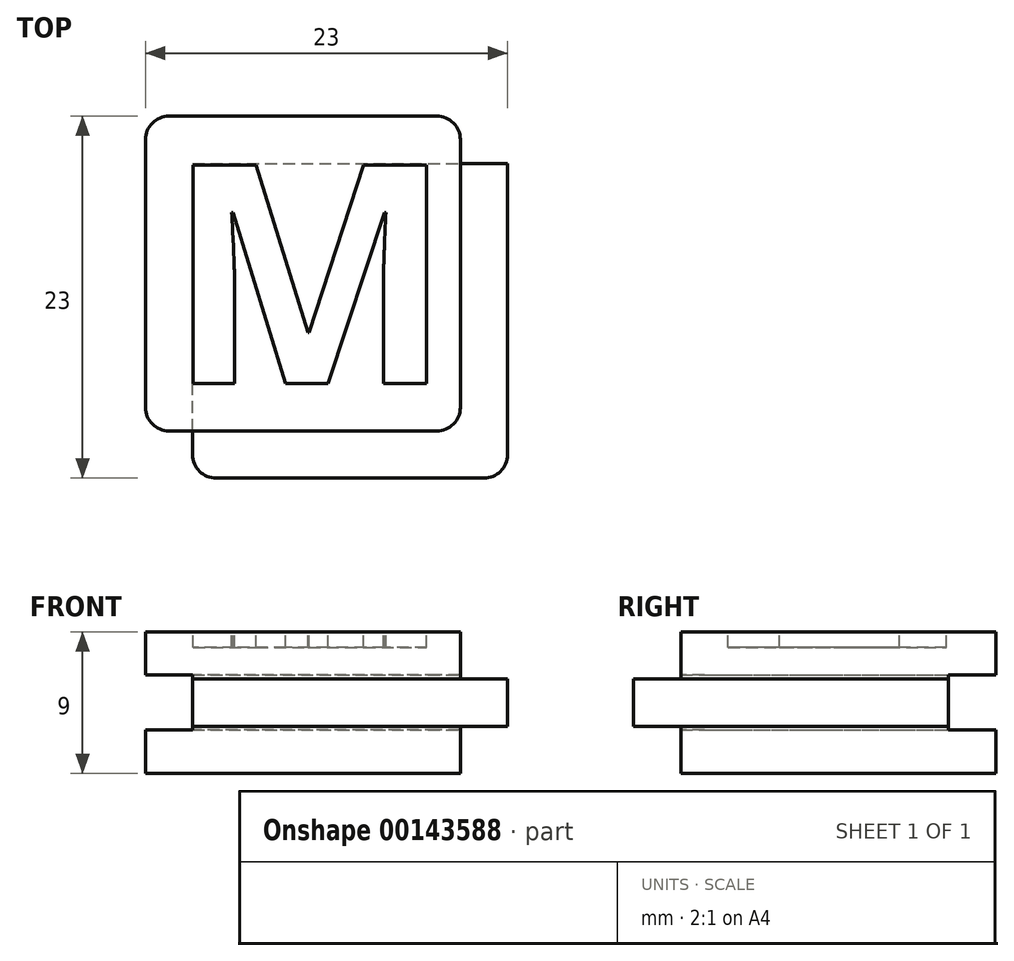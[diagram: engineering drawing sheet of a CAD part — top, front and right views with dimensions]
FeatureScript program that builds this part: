
annotation { "Feature Type Name" : "Feature", "Feature Type Description" : "" }
export const myFeature = defineFeature(function(context is Context, id is Id, definition is map)
    precondition{}
    {
        {
            var Q0;
            Q0=qCreatedBy(makeId("Front.planeOp"),FACE);
            var sketch = newSketch(context, id + "F0", { "sketchPlane" : qUnion([Q0])});
            skLineSegment(sketch, "E0.bottom", {"start": v(10, 4.5) * mm, "end": v(-10, 4.5) * mm});
            skLineSegment(sketch, "E0.top", {"start": v(10, -4.5) * mm, "end": v(-10, -4.5) * mm});
            skLineSegment(sketch, "E0.left", {"start": v(10, 4.5) * mm, "end": v(10, -4.5) * mm});
            skLineSegment(sketch, "E0.right", {"start": v(-10, 4.5) * mm, "end": v(-10, -4.5) * mm});
            skPoint(sketch, "E0.middle", {"position": v(0, 0) * mm});
            skLineSegment(sketch, "E1.bottom", {"start": v(13, 1.5) * mm, "end": v(7, 1.5) * mm});
            skLineSegment(sketch, "E1.top", {"start": v(13, -1.5) * mm, "end": v(7, -1.5) * mm});
            skLineSegment(sketch, "E1.left", {"start": v(13, 1.5) * mm, "end": v(13, -1.5) * mm});
            skLineSegment(sketch, "E1.right", {"start": v(7, 1.5) * mm, "end": v(7, -1.5) * mm});
            skPoint(sketch, "E1.middle", {"position": v(10, 0) * mm});
            skLineSegment(sketch, "E2.bottom", {"start": v(7, 1.5) * mm, "end": v(-7, 1.5) * mm});
            skLineSegment(sketch, "E2.top", {"start": v(7, -1.5) * mm, "end": v(-7, -1.5) * mm});
            skLineSegment(sketch, "E2.right", {"start": v(-7, 1.5) * mm, "end": v(-7, -1.5) * mm});
            skLineSegment(sketch, "E3.bottom", {"start": v(-7, -1.5) * mm, "end": v(-10, -1.5) * mm});
            skLineSegment(sketch, "E3.top", {"start": v(-7, 1.5) * mm, "end": v(-10, 1.5) * mm});
            skLineSegment(sketch, "E3.left", {"start": v(-7, -1.5) * mm, "end": v(-7, 1.5) * mm});
            skLineSegment(sketch, "E3.right", {"start": v(-10, -1.5) * mm, "end": v(-10, 1.5) * mm});
            skSolve(sketch);
        }
        {
            var Q0;
            {var subQ5=sQuery(id+"F0.wireOp",EDGE,"E0.bottom");Q0=makeQuery(id+"F0.imprint","IMPRINT",FACE,{"disambiguationData":[TD([[makeQuery(id+"F0.imprint","IMPRINT",EDGE,{"derivedFrom":subQ5}),1.0]])]});}
            var Q1;
            Q1=makeQuery(id+"F0.imprint","IMPRINT",FACE,{"disambiguationData":[TD([[makeQuery(id+"F0.imprint","IMPRINT",EDGE,{"derivedFrom":sQuery(id+"F0.wireOp",EDGE,"E2.bottom")}),1.0]])]});
            var Q2;
            {var subQ5=sQuery(id+"F0.wireOp",EDGE,"E1.left");Q2=makeQuery(id+"F0.imprint","IMPRINT",FACE,{"disambiguationData":[TD([[makeQuery(id+"F0.imprint","IMPRINT",EDGE,{"derivedFrom":subQ5}),-1.0]])]});}
            var Q3;
            {var subQ5=sQuery(id+"F0.wireOp",EDGE,"E1.right");Q3=makeQuery(id+"F0.imprint","IMPRINT",FACE,{"disambiguationData":[TD([[makeQuery(id+"F0.imprint","IMPRINT",EDGE,{"derivedFrom":subQ5}),1.0]])]});}
            var Q4;
            Q4=makeQuery(id+"F0.imprint","IMPRINT",FACE,{"disambiguationData":[TD([[makeQuery(id+"F0.imprint","IMPRINT",EDGE,{"derivedFrom":sQuery(id+"F0.wireOp",EDGE,"E3.bottom")}),-1.0]])]});
            var Q5;
            {var subQ5=sQuery(id+"F0.wireOp",EDGE,"E0.top");Q5=makeQuery(id+"F0.imprint","IMPRINT",FACE,{"disambiguationData":[TD([[makeQuery(id+"F0.imprint","IMPRINT",EDGE,{"derivedFrom":subQ5}),-1.0]])]});}
            extrude(context, id + "F1", {"entities" : qUnion([Q0, Q1, Q2, Q3, Q4, Q5]), "oppositeDirection" : true, "depth" : 20 * mm});
        }
        {
            var Q0;
            Q0=makeQuery(id+"F0.imprint","IMPRINT",FACE,{"disambiguationData":[TD([[makeQuery(id+"F0.imprint","IMPRINT",EDGE,{"derivedFrom":sQuery(id+"F0.wireOp",EDGE,"E3.bottom")}),-1.0]])]});
            var Q1;
            Q1=makeQuery(id+"F0.imprint","IMPRINT",FACE,{"disambiguationData":[TD([[makeQuery(id+"F0.imprint","IMPRINT",EDGE,{"derivedFrom":sQuery(id+"F0.wireOp",EDGE,"E2.bottom")}),1.0]])]});
            var Q2;
            {var subQ5=sQuery(id+"F0.wireOp",EDGE,"E1.right");Q2=makeQuery(id+"F0.imprint","IMPRINT",FACE,{"disambiguationData":[TD([[makeQuery(id+"F0.imprint","IMPRINT",EDGE,{"derivedFrom":subQ5}),1.0]])]});}
            var Q3;
            {var subQ5=sQuery(id+"F0.wireOp",EDGE,"E1.left");Q3=makeQuery(id+"F0.imprint","IMPRINT",FACE,{"disambiguationData":[TD([[makeQuery(id+"F0.imprint","IMPRINT",EDGE,{"derivedFrom":subQ5}),-1.0]])]});}
            extrude(context, id + "F2", {"entities" : qUnion([Q0, Q1, Q2, Q3]), "operationType" : NewBodyOperationType.ADD, "depth" : 3 * mm});
        }
        {
            var Q0;
            {var subQ0=sQuery(id+"F0.wireOp",EDGE,"E1.left");Q0=makeQuery(id+"F2.boolean.opBoolean","MERGE",FACE,{"derivedFrom":[makeQuery(id+"F1.opExtrude","SWEPT_FACE",FACE,{"disambiguationData":[OSD([subQ0])]}),makeQuery(id+"F2.opExtrude","SWEPT_FACE",FACE,{"disambiguationData":[OSD([subQ0])]})]});}
            var sketch = newSketch(context, id + "F3", { "sketchPlane" : qUnion([Q0])});
            skLineSegment(sketch, "E4.bottom", {"start": v(23, 1.75) * mm, "end": v(17, 1.75) * mm});
            skLineSegment(sketch, "E4.top", {"start": v(23, -1.75) * mm, "end": v(17, -1.75) * mm});
            skLineSegment(sketch, "E4.left", {"start": v(23, 1.75) * mm, "end": v(23, -1.75) * mm});
            skLineSegment(sketch, "E4.right", {"start": v(17, 1.75) * mm, "end": v(17, -1.75) * mm});
            skPoint(sketch, "E4.middle", {"position": v(20, 0) * mm});
            skSolve(sketch);
        }
        {
            var Q0;
            {var subQ1=sQuery(id+"F3.wireOp",EDGE,"E4.bottom");Q0=makeQuery(id+"F3.imprint","IMPRINT",FACE,{"disambiguationData":[TD([[makeQuery(id+"F3.imprint","IMPRINT",EDGE,{"derivedFrom":subQ1}),1.0]])]});}
            var Q1;
            {var subQ1=sQuery(id+"F0.wireOp",EDGE,"E1.left");var subQ8=makeQuery(id+"F1.opExtrude","CAP_EDGE",EDGE,{"disambiguationData":[OSD([subQ1])],"isStart":false});Q1=makeQuery(id+"F3.imprint","IMPRINT",FACE,{"disambiguationData":[TD([[makeQuery(id+"F3.imprint","IMPRINT",EDGE,{"derivedFrom":subQ8}),-1.0]])]});}
            extrude(context, id + "F4", {"entities" : qUnion([Q0, Q1]), "operationType" : NewBodyOperationType.REMOVE, "oppositeDirection" : true, "depth" : 100 * mm});
        }
        {
            var Q0;
            Q0=makeQuery(id+"F4.boolean.opBoolean","COPY",FACE,{"derivedFrom":makeQuery(id+"F4.opExtrude","SWEPT_FACE",FACE,{"disambiguationData":[OSD([sQuery(id+"F3.wireOp",EDGE,"E4.right")])]})});
            var sketch = newSketch(context, id + "F5", { "sketchPlane" : qUnion([Q0])});
            skLineSegment(sketch, "E5.bottom", {"start": v(13, 1.75) * mm, "end": v(7, 1.75) * mm});
            skLineSegment(sketch, "E5.top", {"start": v(13, -1.75) * mm, "end": v(7, -1.75) * mm});
            skLineSegment(sketch, "E5.left", {"start": v(13, 1.75) * mm, "end": v(13, -1.75) * mm});
            skLineSegment(sketch, "E5.right", {"start": v(7, 1.75) * mm, "end": v(7, -1.75) * mm});
            skPoint(sketch, "E5.middle", {"position": v(10, 0) * mm});
            skSolve(sketch);
        }
        {
            var Q0;
            {var subQ3=sQuery(id+"F5.wireOp",EDGE,"E5.left");Q0=makeQuery(id+"F5.imprint","IMPRINT",FACE,{"disambiguationData":[TD([[makeQuery(id+"F5.imprint","IMPRINT",EDGE,{"derivedFrom":subQ3}),-1.0]])]});}
            var Q1;
            {var subQ4=sQuery(id+"F5.wireOp",EDGE,"E5.right");Q1=makeQuery(id+"F5.imprint","IMPRINT",FACE,{"disambiguationData":[TD([[makeQuery(id+"F5.imprint","IMPRINT",EDGE,{"derivedFrom":subQ4}),1.0]])]});}
            extrude(context, id + "F6", {"entities" : qUnion([Q0, Q1]), "operationType" : NewBodyOperationType.REMOVE, "oppositeDirection" : true, "depth" : 100 * mm});
        }
        {
            var Q0;
            Q0=makeQuery(id+"F6.boolean.opBoolean","INTERSECT",EDGE,{"derivedFrom":[makeQuery(id+"F2.opExtrude","CAP_FACE",FACE,{"disambiguationData":[OSD([sQuery(id+"F0.wireOp",EDGE,"E1.bottom"),sQuery(id+"F0.wireOp",EDGE,"E1.top"),sQuery(id+"F0.wireOp",EDGE,"E1.left"),sQuery(id+"F0.wireOp",EDGE,"E2.bottom"),sQuery(id+"F0.wireOp",EDGE,"E2.top"),sQuery(id+"F0.wireOp",EDGE,"E3.bottom"),sQuery(id+"F0.wireOp",EDGE,"E3.top"),sQuery(id+"F0.wireOp",EDGE,"E3.right")])],"isStart":false}),makeQuery(id+"F6.opExtrude","SWEPT_FACE",FACE,{"disambiguationData":[OSD([sQuery(id+"F5.wireOp",EDGE,"E5.right")])]})]});
            var Q1;
            Q1=makeQuery(id+"F2.opExtrude","CAP_EDGE",EDGE,{"disambiguationData":[OSD([sQuery(id+"F0.wireOp",EDGE,"E1.left")])],"isStart":false});
            var Q2;
            {var subQ0=sQuery(id+"F0.wireOp",EDGE,"E0.left");Q2=makeQuery(id+"F1.opExtrude","CAP_EDGE",EDGE,{"disambiguationData":[OSD([subQ0]),TDD([makeQuery(id+"F0.imprint","IMPRINT",EDGE,{"disambiguationData":[TD([[makeQuery(id+"F0.imprint","INTERSECT",VERTEX,{"derivedFrom":[sQuery(id+"F0.wireOp",EDGE,"E0.bottom"),subQ0]}),-1.0]])],"derivedFrom":subQ0})])],"isStart":true});}
            var Q3;
            {var subQ0=sQuery(id+"F0.wireOp",EDGE,"E0.left");Q3=makeQuery(id+"F1.opExtrude","CAP_EDGE",EDGE,{"disambiguationData":[OSD([subQ0]),TDD([makeQuery(id+"F0.imprint","IMPRINT",EDGE,{"disambiguationData":[TD([[makeQuery(id+"F0.imprint","INTERSECT",VERTEX,{"derivedFrom":[sQuery(id+"F0.wireOp",EDGE,"E0.top"),subQ0]}),1.0]])],"derivedFrom":subQ0})])],"isStart":true});}
            var Q4;
            {var subQ0=sQuery(id+"F0.wireOp",EDGE,"E3.right");var subQ1=sQuery(id+"F0.wireOp",EDGE,"E0.right");var subQ3=sQuery(id+"F0.wireOp",EDGE,"E0.top");Q4=makeQuery(id+"F2.boolean.opBoolean","SPLIT",EDGE,{"disambiguationData":[TD([makeQuery(id+"F1.opExtrude","SWEPT_FACE",FACE,{"disambiguationData":[OSD([subQ3])]})])],"derivedFrom":makeQuery(id+"F1.opExtrude","CAP_EDGE",EDGE,{"disambiguationData":[OSD([subQ1,subQ0])],"isStart":true})});}
            var Q5;
            {var subQ1=sQuery(id+"F0.wireOp",EDGE,"E3.right");var subQ2=sQuery(id+"F0.wireOp",EDGE,"E0.right");var subQ3=sQuery(id+"F0.wireOp",EDGE,"E0.bottom");Q5=makeQuery(id+"F2.boolean.opBoolean","SPLIT",EDGE,{"disambiguationData":[TD([makeQuery(id+"F1.opExtrude","SWEPT_FACE",FACE,{"disambiguationData":[OSD([subQ3])]})])],"derivedFrom":makeQuery(id+"F1.opExtrude","CAP_EDGE",EDGE,{"disambiguationData":[OSD([subQ2,subQ1])],"isStart":true})});}
            var Q6;
            Q6=makeQuery(id+"F6.boolean.opBoolean","COPY",EDGE,{"derivedFrom":makeQuery(id+"F6.opExtrude","CAP_EDGE",EDGE,{"disambiguationData":[OSD([sQuery(id+"F5.wireOp",EDGE,"E5.right")])],"isStart":true})});
            var Q7;
            {var subQ0=sQuery(id+"F0.wireOp",EDGE,"E3.right");var subQ1=sQuery(id+"F0.wireOp",EDGE,"E0.right");var subQ2=sQuery(id+"F0.wireOp",EDGE,"E0.bottom");Q7=makeQuery(id+"F4.boolean.opBoolean","SPLIT",EDGE,{"disambiguationData":[TD([makeQuery(id+"F1.opExtrude","SWEPT_FACE",FACE,{"disambiguationData":[OSD([subQ2])]})])],"derivedFrom":makeQuery(id+"F1.opExtrude","CAP_EDGE",EDGE,{"disambiguationData":[OSD([subQ1,subQ0])],"isStart":false})});}
            var Q8;
            {var subQ0=sQuery(id+"F0.wireOp",EDGE,"E3.right");var subQ1=sQuery(id+"F0.wireOp",EDGE,"E0.right");var subQ2=sQuery(id+"F0.wireOp",EDGE,"E0.top");Q8=makeQuery(id+"F4.boolean.opBoolean","SPLIT",EDGE,{"disambiguationData":[TD([makeQuery(id+"F1.opExtrude","SWEPT_FACE",FACE,{"disambiguationData":[OSD([subQ2])]})])],"derivedFrom":makeQuery(id+"F1.opExtrude","CAP_EDGE",EDGE,{"disambiguationData":[OSD([subQ1,subQ0])],"isStart":false})});}
            var Q9;
            Q9=makeQuery(id+"F4.boolean.opBoolean","COPY",EDGE,{"derivedFrom":makeQuery(id+"F4.opExtrude","CAP_EDGE",EDGE,{"disambiguationData":[OSD([sQuery(id+"F3.wireOp",EDGE,"E4.right")])],"isStart":true})});
            var Q10;
            {var subQ0=sQuery(id+"F0.wireOp",EDGE,"E0.left");Q10=makeQuery(id+"F1.opExtrude","CAP_EDGE",EDGE,{"disambiguationData":[OSD([subQ0]),TDD([makeQuery(id+"F0.imprint","IMPRINT",EDGE,{"disambiguationData":[TD([[makeQuery(id+"F0.imprint","INTERSECT",VERTEX,{"derivedFrom":[sQuery(id+"F0.wireOp",EDGE,"E0.bottom"),subQ0]}),-1.0]])],"derivedFrom":subQ0})])],"isStart":false});}
            var Q11;
            {var subQ0=sQuery(id+"F0.wireOp",EDGE,"E0.left");Q11=makeQuery(id+"F1.opExtrude","CAP_EDGE",EDGE,{"disambiguationData":[OSD([subQ0]),TDD([makeQuery(id+"F0.imprint","IMPRINT",EDGE,{"disambiguationData":[TD([[makeQuery(id+"F0.imprint","INTERSECT",VERTEX,{"derivedFrom":[sQuery(id+"F0.wireOp",EDGE,"E0.top"),subQ0]}),1.0]])],"derivedFrom":subQ0})])],"isStart":false});}
            fillet(context, id + "F7", {"entities" : qUnion([Q0, Q1, Q2, Q3, Q4, Q5, Q6, Q7, Q8, Q9, Q10, Q11]), "radius" : 1.5 * mm, "tangentPropagation" : true, "allowEdgeOverflow" : false});
        }
        {
            var Q0;
            Q0=makeQuery(id+"F1.opExtrude","SWEPT_FACE",FACE,{"disambiguationData":[OSD([sQuery(id+"F0.wireOp",EDGE,"E0.bottom")])]});
            var sketch = newSketch(context, id + "F8", { "sketchPlane" : qUnion([Q0])});
            skText(sketch, "E6", { "text": "M", "fontName": "OpenSans-Bold.ttf"});
            skLineSegment(sketch, "E7.0", {"start": v(11.47, 3) * mm, "end": v(-11.07, 3) * mm});
            const initialGuessF8  = {"E6": [-0.00872, 0.003, 1, 0, 0.014]};
            skSetInitialGuess(sketch, initialGuessF8);
            skSolve(sketch);
        }
        {
            var Q0;
            {var subQ0=sQuery(id+"F8.wireOp",EDGE,"E6.sketch_text.stroke-1");Q0=makeQuery(id+"F8.imprint","IMPRINT",FACE,{"disambiguationData":[TD([[makeQuery(id+"F8.imprint","IMPRINT",EDGE,{"derivedFrom":subQ0}),-1.0]])]});}
            extrude(context, id + "F9", {"entities" : qUnion([Q0]), "operationType" : NewBodyOperationType.REMOVE, "oppositeDirection" : true, "depth" : 1 * mm});
        }
    });
